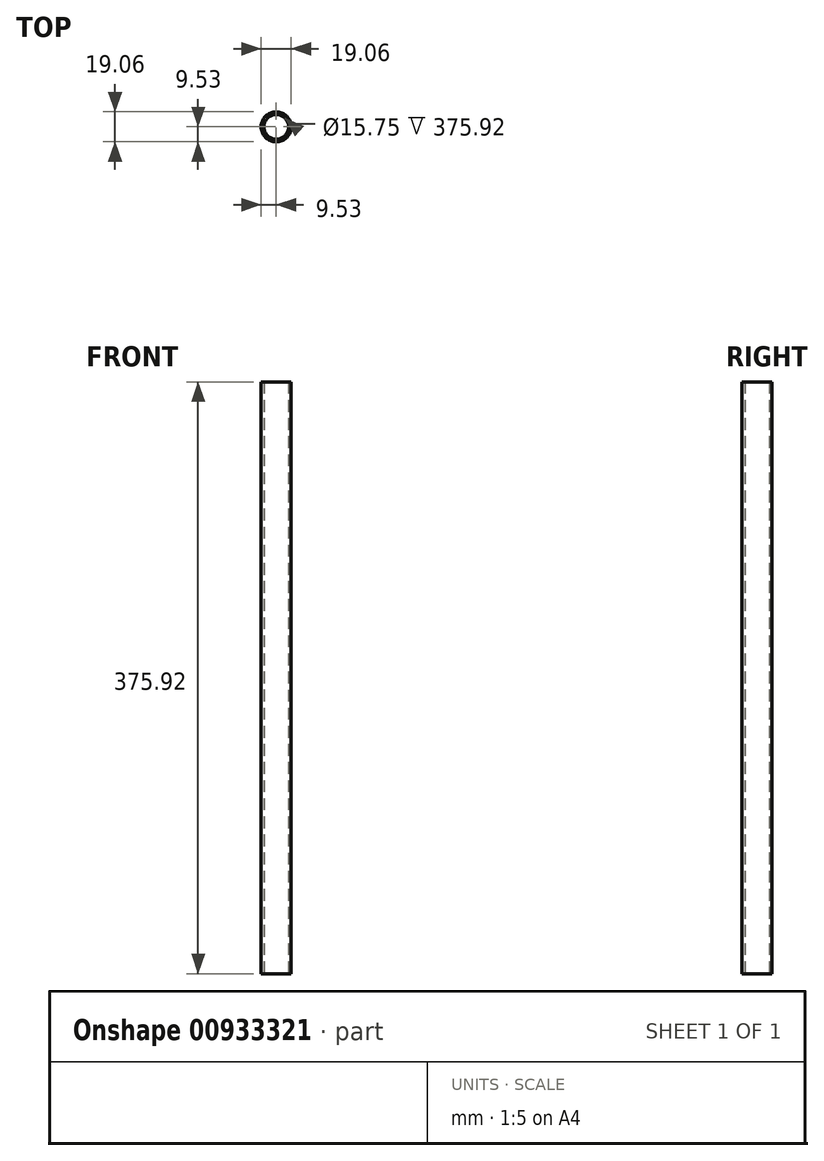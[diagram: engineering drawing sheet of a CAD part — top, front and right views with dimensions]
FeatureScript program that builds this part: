
annotation { "Feature Type Name" : "Feature", "Feature Type Description" : "" }
export const myFeature = defineFeature(function(context is Context, id is Id, definition is map)
    precondition{}
    {
        {
            var Q0;
            Q0=qCreatedBy(makeId("Top.planeOp"),FACE);
            var sketch = newSketch(context, id + "F0", { "sketchPlane" : qUnion([Q0])});
            skCircle(sketch, "E0", {"center": v(0, 0) * mm, "radius": 9.53 * mm});
            skCircle(sketch, "E1", {"center": v(0, 0) * mm, "radius": 7.87 * mm});
            skSolve(sketch);
        }
        {
            var Q0;
            Q0=makeQuery(id+"F0.imprint","IMPRINT",FACE,{"disambiguationData":[TD([[makeQuery(id+"F0.imprint","IMPRINT",EDGE,{"derivedFrom":sQuery(id+"F0.wireOp",EDGE,"E0")}),1.0]])]});
            extrude(context, id + "F1", {"entities" : qUnion([Q0]), "depth" : 375.92 * mm, "offsetDistance" : 25.4 * mm});
        }
    });
